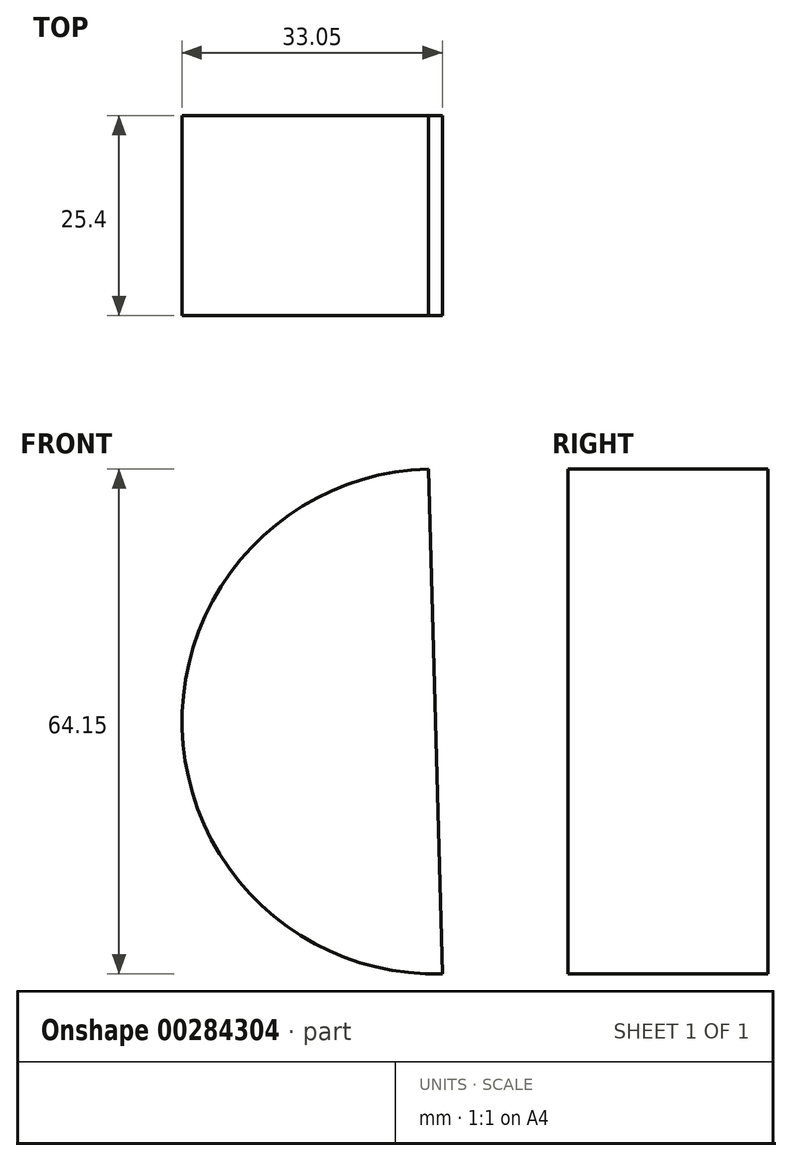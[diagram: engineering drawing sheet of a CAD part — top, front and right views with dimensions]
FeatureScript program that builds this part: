
annotation { "Feature Type Name" : "Feature", "Feature Type Description" : "" }
export const myFeature = defineFeature(function(context is Context, id is Id, definition is map)
    precondition{}
    {
        {
            var Q0;
            Q0=qCreatedBy(makeId("Front.planeOp"),FACE);
            var sketch = newSketch(context, id + "F0", { "sketchPlane" : qUnion([Q0])});
            skArc(sketch, "E0", {"start": v(-41.37, 32.07) * mm, "mid": v(-72.62, -0.89) * mm, "end": v(-39.59, -32.06) * mm});
            skArc(sketch, "E1.MirrorCS", {"start": v(41.37, 32.07) * mm, "mid": v(72.62, -0.89) * mm, "end": v(39.59, -32.06) * mm});
            skLineSegment(sketch, "E2", {"start": v(-41.37, 32.07) * mm, "end": v(-39.59, -32.06) * mm});
            skLineSegment(sketch, "E3", {"start": v(41.37, 32.07) * mm, "end": v(39.59, -32.06) * mm});
            skSolve(sketch);
        }
        {
            var Q0;
            Q0=makeQuery(id+"F0.imprint","IMPRINT",FACE,{"disambiguationData":[TD([[makeQuery(id+"F0.imprint","IMPRINT",EDGE,{"derivedFrom":sQuery(id+"F0.wireOp",EDGE,"E0")}),1.0]])]});
            var Q1;
            Q1=makeQuery(id+"F0.imprint","IMPRINT",FACE,{"disambiguationData":[TD([[makeQuery(id+"F0.imprint","IMPRINT",EDGE,{"derivedFrom":sQuery(id+"F0.wireOp",EDGE,"E1.MirrorCS")}),-1.0]])]});
            extrude(context, id + "F1", {"entities" : qUnion([Q0, Q1]), "depth" : 25.4 * mm});
        }
    });
